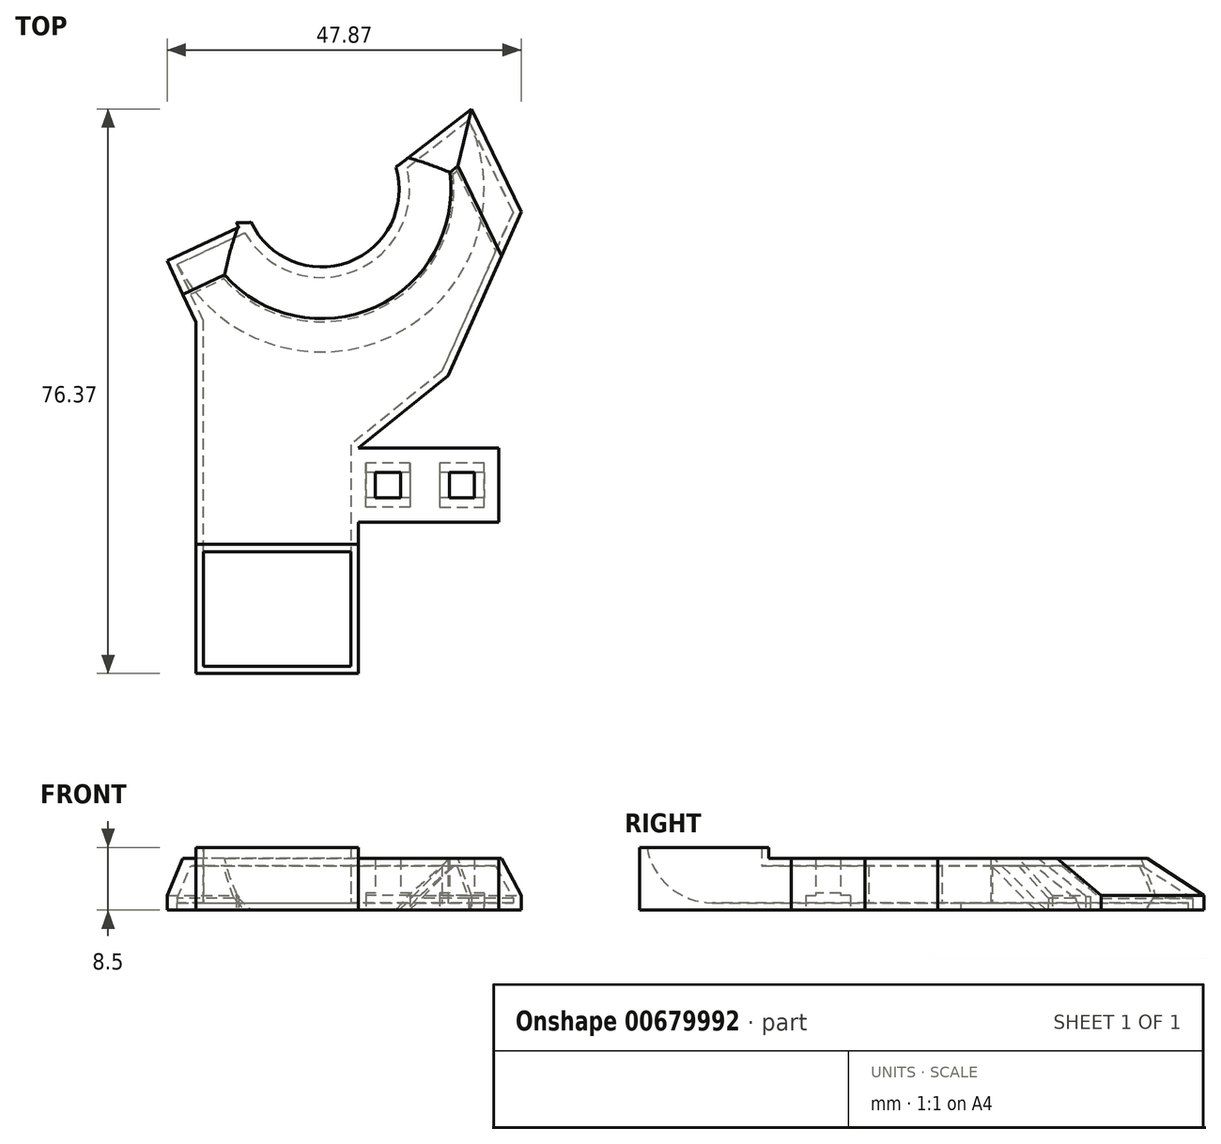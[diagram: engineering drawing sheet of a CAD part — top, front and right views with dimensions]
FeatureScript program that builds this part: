
annotation { "Feature Type Name" : "Feature", "Feature Type Description" : "" }
export const myFeature = defineFeature(function(context is Context, id is Id, definition is map)
    precondition{}
    {
        {
            var Q0;
            Q0=qCreatedBy(makeId("Top.planeOp"),FACE);
            var sketch = newSketch(context, id + "F0", { "sketchPlane" : qUnion([Q0])});
            skLineSegment(sketch, "E0", {"start": v(0, 0) * mm, "end": v(0, -12) * mm, "construction": true});
            skLineSegment(sketch, "E1", {"start": v(0, -12) * mm, "end": v(0, -21.5) * mm, "construction": true});
            skLineSegment(sketch, "E2", {"start": v(0, -12) * mm, "end": v(-5, -12) * mm, "construction": true});
            skLineSegment(sketch, "E3", {"start": v(-5, -12) * mm, "end": v(-15, -12) * mm, "construction": true});
            skLineSegment(sketch, "E4", {"start": v(0, -21.5) * mm, "end": v(-40, -21.5) * mm, "construction": true});
            skPoint(sketch, "E5", {"position": v(-24, 28) * mm});
            skLineSegment(sketch, "E6", {"start": v(-40, -21.5) * mm, "end": v(-40, -36.5) * mm, "construction": true});
            skLineSegment(sketch, "E7", {"start": v(-40, -36.5) * mm, "end": v(-20, -36.5) * mm, "construction": true});
            skLineSegment(sketch, "E8", {"start": v(-20, -36.5) * mm, "end": v(-20, -21.5) * mm, "construction": true});
            skLineSegment(sketch, "E9", {"start": v(-32, 43.5) * mm, "end": v(-32, 23.5) * mm, "construction": true});
            skLineSegment(sketch, "E10", {"start": v(-32, 23.5) * mm, "end": v(-16, 23.5) * mm, "construction": true});
            skLineSegment(sketch, "E11", {"start": v(-16, 23.5) * mm, "end": v(-16, 43.5) * mm, "construction": true});
            skLineSegment(sketch, "E12", {"start": v(-16, 43.5) * mm, "end": v(-32, 43.5) * mm, "construction": true});
            skLineSegment(sketch, "E13", {"start": v(-24, 28) * mm, "end": v(-24, 23.5) * mm, "construction": true});
            skSolve(sketch);
        }
        {
            var Q0;
            Q0=qCreatedBy(makeId("Top.planeOp"),FACE);
            var sketch = newSketch(context, id + "F1", { "sketchPlane" : qUnion([Q0])});
            skLineSegment(sketch, "E14", {"start": v(-19, -7) * mm, "end": v(-19, -17) * mm});
            skLineSegment(sketch, "E15", {"start": v(-19, -17) * mm, "end": v(-19, -37.5) * mm});
            skLineSegment(sketch, "E16", {"start": v(-19, -37.5) * mm, "end": v(-41, -37.5) * mm});
            skLineSegment(sketch, "E17", {"start": v(-41, -37.5) * mm, "end": v(-41, -15) * mm});
            skLineSegment(sketch, "E18", {"start": v(-41, -15) * mm, "end": v(-41, 10) * mm});
            skPoint(sketch, "E19.0", {"position": v(-15, -12) * mm});
            skPoint(sketch, "E20.0", {"position": v(-5, -12) * mm});
            skLineSegment(sketch, "E21.0", {"start": v(-40, -21.5) * mm, "end": v(-40, -36.5) * mm});
            skLineSegment(sketch, "E22.0", {"start": v(-20, -36.5) * mm, "end": v(-20, -21.5) * mm});
            skLineSegment(sketch, "E23.rect.bottom", {"start": v(-12, -10.3) * mm, "end": v(-18, -10.3) * mm});
            skLineSegment(sketch, "E23.rect.top", {"start": v(-12, -13.7) * mm, "end": v(-18, -13.7) * mm});
            skLineSegment(sketch, "E23.rect.left", {"start": v(-12, -10.3) * mm, "end": v(-12, -13.7) * mm});
            skLineSegment(sketch, "E23.rect.right", {"start": v(-18, -10.3) * mm, "end": v(-18, -13.7) * mm});
            skLineSegment(sketch, "E24.rect.bottom", {"start": v(-2, -10.3) * mm, "end": v(-8, -10.3) * mm});
            skLineSegment(sketch, "E24.rect.top", {"start": v(-2, -13.7) * mm, "end": v(-8, -13.7) * mm});
            skLineSegment(sketch, "E24.rect.left", {"start": v(-2, -10.3) * mm, "end": v(-2, -13.7) * mm});
            skLineSegment(sketch, "E24.rect.right", {"start": v(-8, -10.3) * mm, "end": v(-8, -13.7) * mm});
            skLineSegment(sketch, "E25", {"start": v(-8, -10.3) * mm, "end": v(-12, -10.3) * mm, "construction": true});
            skLineSegment(sketch, "E26", {"start": v(-2, -10.3) * mm, "end": v(-2, -9) * mm});
            skLineSegment(sketch, "E27", {"start": v(-2, -9) * mm, "end": v(-8, -9) * mm});
            skLineSegment(sketch, "E28", {"start": v(-8, -9) * mm, "end": v(-8, -10.3) * mm});
            skLineSegment(sketch, "E29", {"start": v(-8, -13.7) * mm, "end": v(-8, -15) * mm});
            skLineSegment(sketch, "E30", {"start": v(-8, -15) * mm, "end": v(-2, -15) * mm});
            skLineSegment(sketch, "E31", {"start": v(-2, -15) * mm, "end": v(-2, -13.7) * mm});
            skLineSegment(sketch, "E32", {"start": v(-12, -10.3) * mm, "end": v(-12, -9) * mm});
            skLineSegment(sketch, "E33", {"start": v(-12, -9) * mm, "end": v(-18, -9) * mm});
            skLineSegment(sketch, "E34", {"start": v(-18, -9) * mm, "end": v(-18, -10.3) * mm});
            skLineSegment(sketch, "E35", {"start": v(-12, -13.7) * mm, "end": v(-12, -15) * mm});
            skLineSegment(sketch, "E36", {"start": v(-12, -15) * mm, "end": v(-18, -15) * mm});
            skLineSegment(sketch, "E37", {"start": v(-18, -15) * mm, "end": v(-18, -13.7) * mm});
            skLineSegment(sketch, "E38.rect.bottom", {"start": v(-13.3, -10.3) * mm, "end": v(-16.7, -10.3) * mm});
            skLineSegment(sketch, "E38.rect.top", {"start": v(-13.3, -13.7) * mm, "end": v(-16.7, -13.7) * mm});
            skLineSegment(sketch, "E38.rect.left", {"start": v(-13.3, -10.3) * mm, "end": v(-13.3, -13.7) * mm});
            skLineSegment(sketch, "E38.rect.right", {"start": v(-16.7, -10.3) * mm, "end": v(-16.7, -13.7) * mm});
            skLineSegment(sketch, "E39.rect.bottom", {"start": v(-3.3, -10.3) * mm, "end": v(-6.7, -10.3) * mm});
            skLineSegment(sketch, "E39.rect.top", {"start": v(-3.3, -13.7) * mm, "end": v(-6.7, -13.7) * mm});
            skLineSegment(sketch, "E39.rect.left", {"start": v(-3.3, -10.3) * mm, "end": v(-3.3, -13.7) * mm});
            skLineSegment(sketch, "E39.rect.right", {"start": v(-6.7, -10.3) * mm, "end": v(-6.7, -13.7) * mm});
            skLineSegment(sketch, "E40", {"start": v(-19, -17) * mm, "end": v(0, -17) * mm});
            skLineSegment(sketch, "E41", {"start": v(0, -17) * mm, "end": v(0, -7) * mm});
            skLineSegment(sketch, "E42", {"start": v(0, -7) * mm, "end": v(-19, -7) * mm});
            skPoint(sketch, "E43.0", {"position": v(-24, 28) * mm});
            skCircle(sketch, "E44", {"center": v(-24, 28) * mm, "radius": 10.5 * mm});
            skCircle(sketch, "E45", {"center": v(-24, 28) * mm, "radius": 23 * mm});
            skLineSegment(sketch, "E46", {"start": v(-41, 10) * mm, "end": v(-44.86, 18.31) * mm});
            skLineSegment(sketch, "E47", {"start": v(-44.86, 18.31) * mm, "end": v(-33.54, 23.6) * mm});
            skLineSegment(sketch, "E48", {"start": v(-13.93, 30.98) * mm, "end": v(-3.73, 38.87) * mm});
            skLineSegment(sketch, "E49", {"start": v(-3.73, 38.87) * mm, "end": v(3.01, 24.93) * mm});
            skLineSegment(sketch, "E50", {"start": v(3.01, 24.93) * mm, "end": v(-6.89, 2.8) * mm});
            skLineSegment(sketch, "E51", {"start": v(-6.89, 2.8) * mm, "end": v(-19, -7) * mm});
            skSolve(sketch);
        }
        {
            var Q0;
            Q0=qCreatedBy(makeId("Top.planeOp"),FACE);
            var sketch = newSketch(context, id + "F2", { "sketchPlane" : qUnion([Q0])});
            skLineSegment(sketch, "E52.0", {"start": v(-32, 23.5) * mm, "end": v(-16, 23.5) * mm});
            skPoint(sketch, "E53.0", {"position": v(-20, -21.5) * mm});
            skPoint(sketch, "E54.0", {"position": v(-40, -21.5) * mm});
            skLineSegment(sketch, "E55", {"start": v(-40, -21.5) * mm, "end": v(-20, -21.5) * mm, "construction": true});
            skLineSegment(sketch, "E56", {"start": v(-30, -21.5) * mm, "end": v(-24, 23.5) * mm, "construction": true});
            skCircle(sketch, "E57.0", {"center": v(-24, 28) * mm, "radius": 10.5 * mm});
            skLineSegment(sketch, "E58", {"start": v(-12.5, 23.5) * mm, "end": v(-26.67, 3.5) * mm});
            skLineSegment(sketch, "E59", {"start": v(-16, 23.5) * mm, "end": v(-12.5, 23.5) * mm});
            skLineSegment(sketch, "E60", {"start": v(-32, 23.5) * mm, "end": v(-35.5, 23.5) * mm});
            skLineSegment(sketch, "E61", {"start": v(-35.5, 23.5) * mm, "end": v(-26.67, 3.5) * mm});
            skSolve(sketch);
        }
        {
            var Q0;
            Q0=makeQuery(id+"F1.imprint","IMPRINT",FACE,{"disambiguationData":[TD([[makeQuery(id+"F1.imprint","IMPRINT",EDGE,{"derivedFrom":sQuery(id+"F1.wireOp",EDGE,"E14")}),-1.0]])]});
            var Q1;
            {var subQ0=sQuery(id+"F1.wireOp",EDGE,"E47");Q1=makeQuery(id+"F1.imprint","IMPRINT",FACE,{"disambiguationData":[TD([[makeQuery(id+"F1.imprint","IMPRINT",EDGE,{"derivedFrom":subQ0}),-1.0]])]});}
            extrude(context, id + "F3", {"entities" : qUnion([Q0, Q1]), "depth" : 7 * mm});
        }
        {
            var Q0;
            Q0=makeQuery(id+"F3.opExtrude","CAP_FACE",FACE,{"disambiguationData":[OSD([sQuery(id+"F1.wireOp",EDGE,"726e78eb-56e2-47ea-b6f5-47efc0460c47"),sQuery(id+"F1.wireOp",EDGE,"fa15ef6f-fb31-48d0-98cb-08a9dc3e37e7"),sQuery(id+"F1.wireOp",EDGE,"288b6f4e-36c9-46e4-8515-fd5ad4e604e2"),sQuery(id+"F1.wireOp",EDGE,"37ce52b8-0f7f-4cb6-b0b0-6c3cf62d658f"),sQuery(id+"F1.wireOp",EDGE,"6ad6b573-81d0-4507-a461-966eaf882e56"),sQuery(id+"F1.wireOp",EDGE,"1b400430-0135-404f-adc2-64bbd31526d7"),sQuery(id+"F1.wireOp",EDGE,"E14"),sQuery(id+"F1.wireOp",EDGE,"E15"),sQuery(id+"F1.wireOp",EDGE,"E16"),sQuery(id+"F1.wireOp",EDGE,"E17"),sQuery(id+"F1.wireOp",EDGE,"E18"),sQuery(id+"F1.wireOp",EDGE,"71707b2f-24f5-41ae-93e4-82e1504ae774")])],"isStart":false});
            var sketch = newSketch(context, id + "F4", { "sketchPlane" : qUnion([Q0])});
            skLineSegment(sketch, "E62.0", {"start": v(-19, -7) * mm, "end": v(-19, -37.5) * mm});
            skLineSegment(sketch, "E63.0", {"start": v(-19, -37.5) * mm, "end": v(-41, -37.5) * mm});
            skLineSegment(sketch, "E64.0", {"start": v(-41, -37.5) * mm, "end": v(-41, -37.5) * mm});
            skLineSegment(sketch, "E65.0", {"start": v(0, -21.5) * mm, "end": v(-40, -21.5) * mm});
            skLineSegment(sketch, "E66", {"start": v(-19, -20) * mm, "end": v(-41, -20) * mm});
            skSolve(sketch);
        }
        {
            var Q0;
            {var subQ2=sQuery(id+"F4.wireOp",EDGE,"E63.0");Q0=makeQuery(id+"F4.imprint","IMPRINT",FACE,{"disambiguationData":[TD([[makeQuery(id+"F4.imprint","IMPRINT",EDGE,{"derivedFrom":subQ2}),-1.0]])]});}
            extrude(context, id + "F5", {"entities" : qUnion([Q0]), "operationType" : NewBodyOperationType.ADD, "depth" : 1.5 * mm});
        }
        {
            var Q0;
            {var subQ5=sQuery(id+"F2.wireOp",EDGE,"E58");Q0=makeQuery(id+"F2.imprint","IMPRINT",FACE,{"disambiguationData":[TD([[makeQuery(id+"F2.imprint","IMPRINT",EDGE,{"derivedFrom":subQ5}),-1.0]])]});}
            var Q1;
            Q1=makeQuery(id+"F3.opExtrude","CAP_FACE",FACE,{"disambiguationData":[OSD([sQuery(id+"F1.wireOp",EDGE,"E14"),sQuery(id+"F1.wireOp",EDGE,"E15"),sQuery(id+"F1.wireOp",EDGE,"E16"),sQuery(id+"F1.wireOp",EDGE,"E17"),sQuery(id+"F1.wireOp",EDGE,"E18"),sQuery(id+"F1.wireOp",EDGE,"E44"),sQuery(id+"F1.wireOp",EDGE,"E46"),sQuery(id+"F1.wireOp",EDGE,"E47"),sQuery(id+"F1.wireOp",EDGE,"E48"),sQuery(id+"F1.wireOp",EDGE,"E49"),sQuery(id+"F1.wireOp",EDGE,"E50"),sQuery(id+"F1.wireOp",EDGE,"E51")])],"isStart":false});
            extrude(context, id + "F6", {"entities" : qUnion([Q0]), "endBound" : BoundingType.UP_TO_SURFACE, "endBoundEntityFace" : qUnion([Q1]), "depth" : 25 * mm});
        }
        {
            var Q0;
            Q0=makeQuery(id+"F3.opExtrude","CAP_EDGE",EDGE,{"disambiguationData":[OSD([sQuery(id+"F1.wireOp",EDGE,"E44")])],"isStart":false});
            var Q1;
            Q1=makeQuery(id+"F6.opExtrude","CAP_EDGE",EDGE,{"disambiguationData":[OSD([sQuery(id+"F2.wireOp",EDGE,"E57.0")])],"isStart":false});
            chamfer(context, id + "F7", {"entities" : qUnion([Q0, Q1]), "width" : 7 * mm, "tangentPropagation" : true});
        }
        {
            var Q0;
            Q0=makeQuery(id+"F3.opExtrude","CAP_EDGE",EDGE,{"disambiguationData":[OSD([sQuery(id+"F1.wireOp",EDGE,"E47")])],"isStart":false});
            var Q1;
            Q1=makeQuery(id+"F3.opExtrude","CAP_EDGE",EDGE,{"disambiguationData":[OSD([sQuery(id+"F1.wireOp",EDGE,"E49")])],"isStart":false});
            var Q2;
            Q2=makeQuery(id+"F3.opExtrude","CAP_EDGE",EDGE,{"disambiguationData":[OSD([sQuery(id+"F1.wireOp",EDGE,"E48")])],"isStart":false});
            chamfer(context, id + "F8", {"entities" : qUnion([Q0, Q1, Q2]), "width" : 5 * mm, "tangentPropagation" : true});
        }
        {
            var Q0;
            Q0=qCreatedBy(makeId("Top.planeOp"),FACE);
            var sketch = newSketch(context, id + "F9", { "sketchPlane" : qUnion([Q0])});
            skCircle(sketch, "E67.0", {"center": v(-24, 28) * mm, "radius": 23 * mm});
            skCircle(sketch, "E68.0", {"center": v(-24, 28) * mm, "radius": 10.5 * mm});
            skLineSegment(sketch, "E69.0", {"start": v(-44.86, 18.31) * mm, "end": v(-33.54, 23.6) * mm});
            skLineSegment(sketch, "E70.0", {"start": v(-13.93, 30.98) * mm, "end": v(-3.73, 38.87) * mm});
            skSolve(sketch);
        }
        {
            var Q0;
            Q0=qSketchRegion(id+"F9",true);
            extrude(context, id + "F10", {"entities" : qUnion([Q0]), "operationType" : NewBodyOperationType.ADD, "oppositeDirection" : true, "depth" : 5 * mm});
        }
        {
            var Q0;
            Q0=makeQuery(id+"F10.opExtrude","CAP_FACE",FACE,{"disambiguationData":[OSD([sQuery(id+"F9.wireOp",EDGE,"1a944d00-084b-4ff9-9d19-91ccdd1f2c37.0"),sQuery(id+"F9.wireOp",EDGE,"9bbf65b2-a4d8-46b0-b6b6-1e68403ac3ce.0"),sQuery(id+"F9.wireOp",EDGE,"9d110ad1-58db-4db0-9e68-2a1495851d6b.0"),sQuery(id+"F9.wireOp",EDGE,"a38a0b3c-3594-412f-ae05-99f41588887f.0"),sQuery(id+"F9.wireOp",EDGE,"e33504a2-dc81-4a30-935b-ee4b6f65ec9a.0"),sQuery(id+"F9.wireOp",EDGE,"dfe0c6c7-b4f3-4899-ac4e-a66b8dc6344a.0"),sQuery(id+"F9.wireOp",EDGE,"97433154-32f2-4662-a443-5944fef1a110.0"),sQuery(id+"F9.wireOp",EDGE,"175b2ed6-e2aa-4d11-89b4-9663bcb69172")])],"isStart":false});
            var Q1;
            Q1=makeQuery(id+"F5.opExtrude","CAP_FACE",FACE,{"disambiguationData":[OSD([sQuery(id+"F4.wireOp",EDGE,"E62.0"),sQuery(id+"F4.wireOp",EDGE,"E63.0"),sQuery(id+"F4.wireOp",EDGE,"E64.0"),sQuery(id+"F4.wireOp",EDGE,"E66")])],"isStart":false});
            var Q2;
            Q2=makeQuery(id+"F3.opExtrude","SWEPT_BODY",BODY,{"disambiguationData":[OSD([sQuery(id+"F1.wireOp",EDGE,"726e78eb-56e2-47ea-b6f5-47efc0460c47"),sQuery(id+"F1.wireOp",EDGE,"fa15ef6f-fb31-48d0-98cb-08a9dc3e37e7"),sQuery(id+"F1.wireOp",EDGE,"288b6f4e-36c9-46e4-8515-fd5ad4e604e2"),sQuery(id+"F1.wireOp",EDGE,"37ce52b8-0f7f-4cb6-b0b0-6c3cf62d658f"),sQuery(id+"F1.wireOp",EDGE,"6ad6b573-81d0-4507-a461-966eaf882e56"),sQuery(id+"F1.wireOp",EDGE,"1b400430-0135-404f-adc2-64bbd31526d7"),sQuery(id+"F1.wireOp",EDGE,"E14"),sQuery(id+"F1.wireOp",EDGE,"E15"),sQuery(id+"F1.wireOp",EDGE,"E16"),sQuery(id+"F1.wireOp",EDGE,"E17"),sQuery(id+"F1.wireOp",EDGE,"E18"),sQuery(id+"F1.wireOp",EDGE,"71707b2f-24f5-41ae-93e4-82e1504ae774")])]});
            shell(context, id + "F11", {"entities" : qUnion([Q0, Q1]), "parts" : qUnion([Q2]), "thickness" : 1 * mm});
        }
        {
            var Q0;
            Q0=qCreatedBy(makeId("Right.planeOp"),FACE);
            var sketch = newSketch(context, id + "F12", { "sketchPlane" : qUnion([Q0])});
            skLineSegment(sketch, "E71", {"start": v(-51.08, 0) * mm, "end": v(58.7, 0) * mm});
            skLineSegment(sketch, "E72", {"start": v(58.7, 0) * mm, "end": v(58.7, -26.43) * mm});
            skLineSegment(sketch, "E73", {"start": v(58.7, -26.43) * mm, "end": v(-51.08, -26.43) * mm});
            skLineSegment(sketch, "E74", {"start": v(-51.08, -26.43) * mm, "end": v(-51.08, 0) * mm});
            skSolve(sketch);
        }
        {
            var Q0;
            Q0=qSketchRegion(id+"F12",true);
            extrude(context, id + "F13", {"entities" : qUnion([Q0]), "operationType" : NewBodyOperationType.REMOVE, "oppositeDirection" : true, "depth" : 100 * mm, "hasSecondDirection" : true, "secondDirectionOppositeDirection" : false, "secondDirectionDepth" : 100 * mm});
        }
        {
            var Q0;
            Q0=makeQuery(id+"F11.opShell","OFFSET_EDGE",EDGE,{"disambiguationData":[OSD([sQuery(id+"F1.wireOp",EDGE,"E16")])]});
            fillet(context, id + "F14", {"entities" : qUnion([Q0]), "radius" : 9 * mm, "tangentPropagation" : true, "allowEdgeOverflow" : false});
        }
        {
            var Q0;
            {var subQ1=sQuery(id+"F1.wireOp",EDGE,"E23.rect.left");Q0=makeQuery(id+"F1.imprint","IMPRINT",FACE,{"disambiguationData":[TD([[makeQuery(id+"F1.imprint","IMPRINT",EDGE,{"derivedFrom":subQ1}),-1.0]])]});}
            var Q1;
            {var subQ3=sQuery(id+"F1.wireOp",EDGE,"E35");Q1=makeQuery(id+"F1.imprint","IMPRINT",FACE,{"disambiguationData":[TD([[makeQuery(id+"F1.imprint","IMPRINT",EDGE,{"derivedFrom":subQ3}),-1.0]])]});}
            var Q2;
            {var subQ3=sQuery(id+"F1.wireOp",EDGE,"E32");Q2=makeQuery(id+"F1.imprint","IMPRINT",FACE,{"disambiguationData":[TD([[makeQuery(id+"F1.imprint","IMPRINT",EDGE,{"derivedFrom":subQ3}),1.0]])]});}
            var Q3;
            {var subQ1=sQuery(id+"F1.wireOp",EDGE,"E23.rect.right");Q3=makeQuery(id+"F1.imprint","IMPRINT",FACE,{"disambiguationData":[TD([[makeQuery(id+"F1.imprint","IMPRINT",EDGE,{"derivedFrom":subQ1}),1.0]])]});}
            var Q4;
            Q4=makeQuery(id+"F1.imprint","IMPRINT",FACE,{"disambiguationData":[TD([[makeQuery(id+"F1.imprint","IMPRINT",EDGE,{"derivedFrom":sQuery(id+"F1.wireOp",EDGE,"E14")}),1.0]])]});
            var Q5;
            {var subQ1=sQuery(id+"F1.wireOp",EDGE,"E24.rect.right");Q5=makeQuery(id+"F1.imprint","IMPRINT",FACE,{"disambiguationData":[TD([[makeQuery(id+"F1.imprint","IMPRINT",EDGE,{"derivedFrom":subQ1}),1.0]])]});}
            var Q6;
            {var subQ2=sQuery(id+"F1.wireOp",EDGE,"E26");Q6=makeQuery(id+"F1.imprint","IMPRINT",FACE,{"disambiguationData":[TD([[makeQuery(id+"F1.imprint","IMPRINT",EDGE,{"derivedFrom":subQ2}),1.0]])]});}
            var Q7;
            {var subQ0=sQuery(id+"F1.wireOp",EDGE,"E24.rect.left");Q7=makeQuery(id+"F1.imprint","IMPRINT",FACE,{"disambiguationData":[TD([[makeQuery(id+"F1.imprint","IMPRINT",EDGE,{"derivedFrom":subQ0}),-1.0]])]});}
            var Q8;
            {var subQ3=sQuery(id+"F1.wireOp",EDGE,"E29");Q8=makeQuery(id+"F1.imprint","IMPRINT",FACE,{"disambiguationData":[TD([[makeQuery(id+"F1.imprint","IMPRINT",EDGE,{"derivedFrom":subQ3}),1.0]])]});}
            extrude(context, id + "F15", {"entities" : qUnion([Q0, Q1, Q2, Q3, Q4, Q5, Q6, Q7, Q8]), "operationType" : NewBodyOperationType.ADD, "depth" : 7 * mm});
        }
        {
            var Q0;
            {var subQ3=sQuery(id+"F1.wireOp",EDGE,"E32");Q0=makeQuery(id+"F1.imprint","IMPRINT",FACE,{"disambiguationData":[TD([[makeQuery(id+"F1.imprint","IMPRINT",EDGE,{"derivedFrom":subQ3}),1.0]])]});}
            var Q1;
            {var subQ3=sQuery(id+"F1.wireOp",EDGE,"E35");Q1=makeQuery(id+"F1.imprint","IMPRINT",FACE,{"disambiguationData":[TD([[makeQuery(id+"F1.imprint","IMPRINT",EDGE,{"derivedFrom":subQ3}),-1.0]])]});}
            var Q2;
            {var subQ3=sQuery(id+"F1.wireOp",EDGE,"E29");Q2=makeQuery(id+"F1.imprint","IMPRINT",FACE,{"disambiguationData":[TD([[makeQuery(id+"F1.imprint","IMPRINT",EDGE,{"derivedFrom":subQ3}),1.0]])]});}
            var Q3;
            {var subQ2=sQuery(id+"F1.wireOp",EDGE,"E26");Q3=makeQuery(id+"F1.imprint","IMPRINT",FACE,{"disambiguationData":[TD([[makeQuery(id+"F1.imprint","IMPRINT",EDGE,{"derivedFrom":subQ2}),1.0]])]});}
            extrude(context, id + "F16", {"entities" : qUnion([Q0, Q1, Q2, Q3]), "operationType" : NewBodyOperationType.REMOVE, "depth" : (7 - 5) * mm});
        }
        {
            var Q0;
            {var subQ0=sQuery(id+"F1.wireOp",EDGE,"E24.rect.left");Q0=makeQuery(id+"F1.imprint","IMPRINT",FACE,{"disambiguationData":[TD([[makeQuery(id+"F1.imprint","IMPRINT",EDGE,{"derivedFrom":subQ0}),-1.0]])]});}
            var Q1;
            {var subQ1=sQuery(id+"F1.wireOp",EDGE,"E24.rect.right");Q1=makeQuery(id+"F1.imprint","IMPRINT",FACE,{"disambiguationData":[TD([[makeQuery(id+"F1.imprint","IMPRINT",EDGE,{"derivedFrom":subQ1}),1.0]])]});}
            var Q2;
            {var subQ1=sQuery(id+"F1.wireOp",EDGE,"E23.rect.left");Q2=makeQuery(id+"F1.imprint","IMPRINT",FACE,{"disambiguationData":[TD([[makeQuery(id+"F1.imprint","IMPRINT",EDGE,{"derivedFrom":subQ1}),-1.0]])]});}
            var Q3;
            {var subQ1=sQuery(id+"F1.wireOp",EDGE,"E23.rect.right");Q3=makeQuery(id+"F1.imprint","IMPRINT",FACE,{"disambiguationData":[TD([[makeQuery(id+"F1.imprint","IMPRINT",EDGE,{"derivedFrom":subQ1}),1.0]])]});}
            extrude(context, id + "F17", {"entities" : qUnion([Q0, Q1, Q2, Q3]), "operationType" : NewBodyOperationType.REMOVE, "depth" : (7 - 4.7) * mm});
        }
    });
